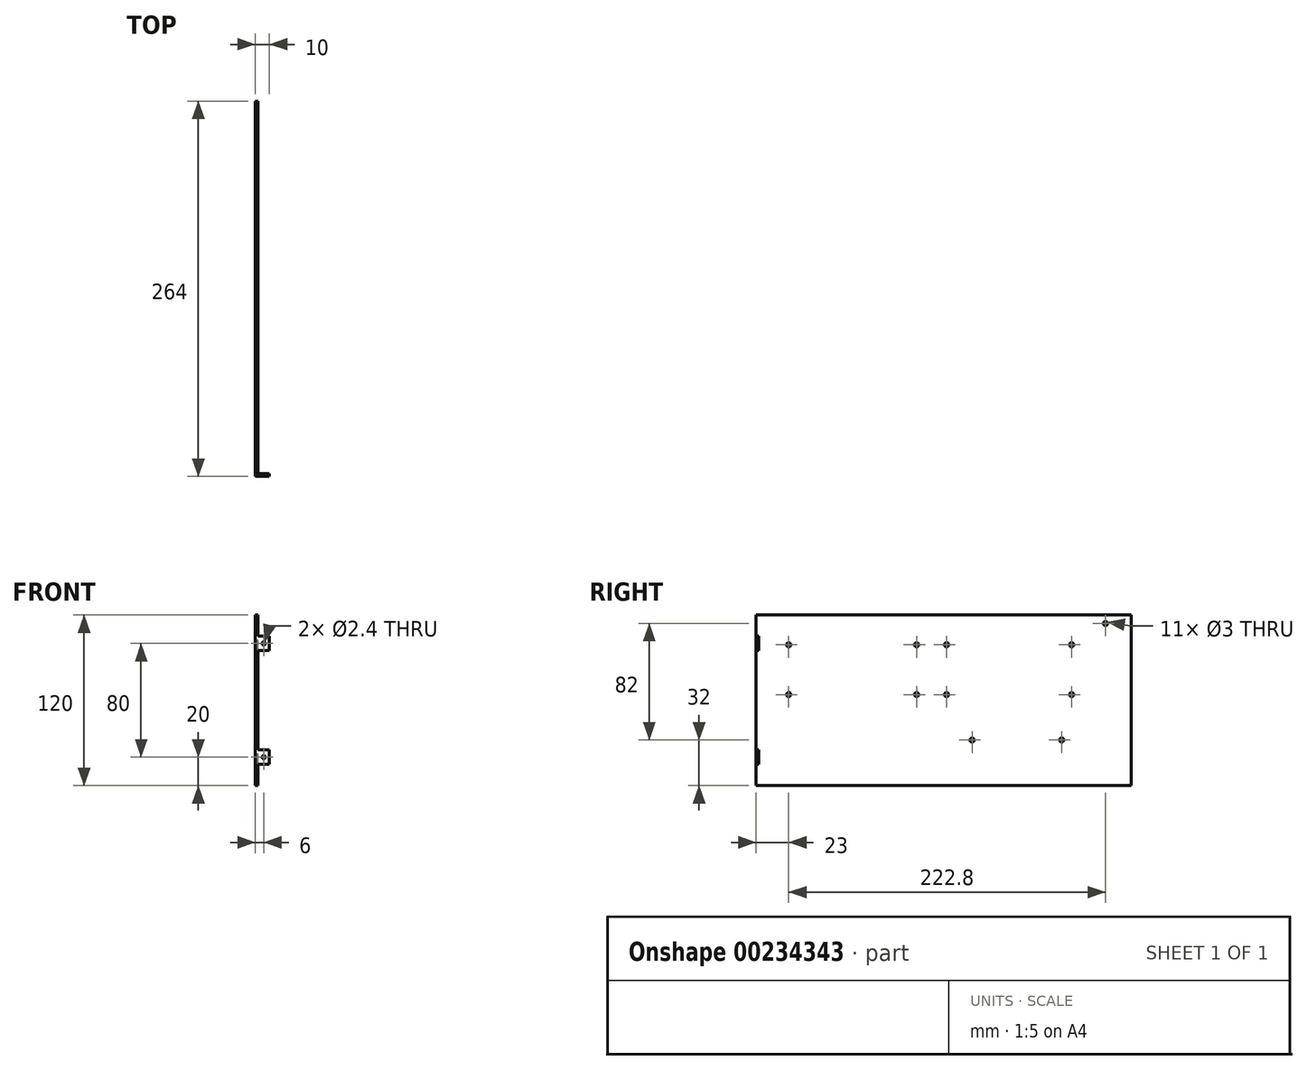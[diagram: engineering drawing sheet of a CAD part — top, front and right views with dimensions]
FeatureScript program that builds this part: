
annotation { "Feature Type Name" : "Feature", "Feature Type Description" : "" }
export const myFeature = defineFeature(function(context is Context, id is Id, definition is map)
    precondition{}
    {
        {
            var Q0;
            Q0=qCreatedBy(makeId("Right.planeOp"),FACE);
            var sketch = newSketch(context, id + "F0", { "sketchPlane" : qUnion([Q0])});
            skLineSegment(sketch, "E0.bottom", {"start": v(132, -60) * mm, "end": v(-132, -60) * mm});
            skLineSegment(sketch, "E0.top", {"start": v(132, 60) * mm, "end": v(-132, 60) * mm});
            skLineSegment(sketch, "E0.left", {"start": v(132, -60) * mm, "end": v(132, 60) * mm});
            skLineSegment(sketch, "E0.right", {"start": v(-132, -60) * mm, "end": v(-132, 60) * mm});
            skPoint(sketch, "E0.middle", {"position": v(0, 0) * mm});
            skLineSegment(sketch, "E1", {"start": v(-132, 40) * mm, "end": v(-120.52, 40) * mm, "construction": true});
            skLineSegment(sketch, "E2", {"start": v(-120.52, -40) * mm, "end": v(-132, -40) * mm, "construction": true});
            skLineSegment(sketch, "E3", {"start": v(-132, 45) * mm, "end": v(-130.2, 45) * mm});
            skLineSegment(sketch, "E4", {"start": v(-130.2, 45) * mm, "end": v(-130.2, 40) * mm});
            skLineSegment(sketch, "E5", {"start": v(-130.2, 40) * mm, "end": v(-130.2, 35) * mm});
            skLineSegment(sketch, "E6", {"start": v(-130.2, 35) * mm, "end": v(-132, 35) * mm});
            skLineSegment(sketch, "E7", {"start": v(-132, -35) * mm, "end": v(-130.2, -35) * mm});
            skLineSegment(sketch, "E8", {"start": v(-130.2, -35) * mm, "end": v(-130.2, -40) * mm});
            skLineSegment(sketch, "E9", {"start": v(-130.2, -40) * mm, "end": v(-130.2, -45) * mm});
            skLineSegment(sketch, "E10", {"start": v(-130.2, -45) * mm, "end": v(-132, -45) * mm});
            skCircle(sketch, "E11", {"center": v(-109, 39) * mm, "radius": 1.5 * mm});
            skCircle(sketch, "E12", {"center": v(-19, 39) * mm, "radius": 1.5 * mm});
            skCircle(sketch, "E13", {"center": v(-109, 4) * mm, "radius": 1.5 * mm});
            skCircle(sketch, "E14", {"center": v(-19, 4) * mm, "radius": 1.5 * mm});
            skCircle(sketch, "E15", {"center": v(2, 39) * mm, "radius": 1.5 * mm});
            skCircle(sketch, "E16", {"center": v(90, 39) * mm, "radius": 1.5 * mm});
            skCircle(sketch, "E17", {"center": v(90, 4) * mm, "radius": 1.5 * mm});
            skCircle(sketch, "E18", {"center": v(2, 4) * mm, "radius": 1.5 * mm});
            skCircle(sketch, "E19", {"center": v(20, -28) * mm, "radius": 1.5 * mm});
            skCircle(sketch, "E20", {"center": v(83, -28) * mm, "radius": 1.5 * mm});
            skCircle(sketch, "E21", {"center": v(113.8, 54) * mm, "radius": 1.5 * mm});
            skSolve(sketch);
        }
        {
            var Q0;
            Q0=makeQuery(id+"F0.imprint","IMPRINT",FACE,{"disambiguationData":[TD([[makeQuery(id+"F0.imprint","IMPRINT",EDGE,{"derivedFrom":sQuery(id+"F0.wireOp",EDGE,"E0.bottom")}),-1.0]])]});
            var Q1;
            {var subQ0=sQuery(id+"F0.wireOp",EDGE,"E3");Q1=makeQuery(id+"F0.imprint","IMPRINT",FACE,{"disambiguationData":[TD([[makeQuery(id+"F0.imprint","IMPRINT",EDGE,{"derivedFrom":subQ0}),-1.0]])]});}
            var Q2;
            {var subQ0=sQuery(id+"F0.wireOp",EDGE,"E7");Q2=makeQuery(id+"F0.imprint","IMPRINT",FACE,{"disambiguationData":[TD([[makeQuery(id+"F0.imprint","IMPRINT",EDGE,{"derivedFrom":subQ0}),-1.0]])]});}
            extrude(context, id + "F1", {"entities" : qUnion([Q0, Q1, Q2]), "depth" : 1.8 * mm});
        }
        {
            var Q0;
            {var subQ0=sQuery(id+"F0.wireOp",EDGE,"E3");Q0=makeQuery(id+"F0.imprint","IMPRINT",FACE,{"disambiguationData":[TD([[makeQuery(id+"F0.imprint","IMPRINT",EDGE,{"derivedFrom":subQ0}),-1.0]])]});}
            var Q1;
            {var subQ0=sQuery(id+"F0.wireOp",EDGE,"E7");Q1=makeQuery(id+"F0.imprint","IMPRINT",FACE,{"disambiguationData":[TD([[makeQuery(id+"F0.imprint","IMPRINT",EDGE,{"derivedFrom":subQ0}),-1.0]])]});}
            extrude(context, id + "F2", {"entities" : qUnion([Q0, Q1]), "operationType" : NewBodyOperationType.ADD, "depth" : 10 * mm});
        }
        {
            var Q0;
            {var subQ0=sQuery(id+"F0.wireOp",EDGE,"E0.right");Q0=makeQuery(id+"F2.boolean.opBoolean","MERGE",FACE,{"derivedFrom":[makeQuery(id+"F1.opExtrude","SWEPT_FACE",FACE,{"disambiguationData":[OSD([subQ0])]}),makeQuery(id+"F2.opExtrude","SWEPT_FACE",FACE,{"disambiguationData":[OSD([subQ0]),TDD([makeQuery(id+"F0.imprint","IMPRINT",EDGE,{"disambiguationData":[TD([[makeQuery(id+"F0.imprint","INTERSECT",VERTEX,{"derivedFrom":[subQ0,sQuery(id+"F0.wireOp",EDGE,"E7")]}),1.0]])],"derivedFrom":subQ0})])]}),makeQuery(id+"F2.opExtrude","SWEPT_FACE",FACE,{"disambiguationData":[OSD([subQ0]),TDD([makeQuery(id+"F0.imprint","IMPRINT",EDGE,{"disambiguationData":[TD([[makeQuery(id+"F0.imprint","INTERSECT",VERTEX,{"derivedFrom":[subQ0,sQuery(id+"F0.wireOp",EDGE,"E3")]}),1.0]])],"derivedFrom":subQ0})])]})]});}
            var sketch = newSketch(context, id + "F3", { "sketchPlane" : qUnion([Q0])});
            skCircle(sketch, "E22", {"center": v(6, 40) * mm, "radius": 1.2 * mm});
            skPoint(sketch, "E22.centerSnap0", {"position": v(10, 40) * mm});
            skCircle(sketch, "E23", {"center": v(6, -40) * mm, "radius": 1.2 * mm});
            skSolve(sketch);
        }
        {
            var Q0;
            Q0=makeQuery(id+"F3.imprint","IMPRINT",FACE,{"disambiguationData":[TD([[makeQuery(id+"F3.imprint","IMPRINT",EDGE,{"derivedFrom":sQuery(id+"F3.wireOp",EDGE,"E22")}),1.0]])]});
            var Q1;
            Q1=makeQuery(id+"F3.imprint","IMPRINT",FACE,{"disambiguationData":[TD([[makeQuery(id+"F3.imprint","IMPRINT",EDGE,{"derivedFrom":sQuery(id+"F3.wireOp",EDGE,"E23")}),1.0]])]});
            var Q2;
            Q2=sQuery(id+"F3.wireOp",EDGE,"E22");
            var Q3;
            Q3=sQuery(id+"F3.wireOp",EDGE,"E23");
            extrude(context, id + "F4", {"entities" : qUnion([Q0, Q1]), "operationType" : NewBodyOperationType.REMOVE, "surfaceEntities" : qUnion([Q2, Q3]), "endBound" : BoundingType.THROUGH_ALL, "oppositeDirection" : true, "depth" : 25 * mm});
        }
    });
